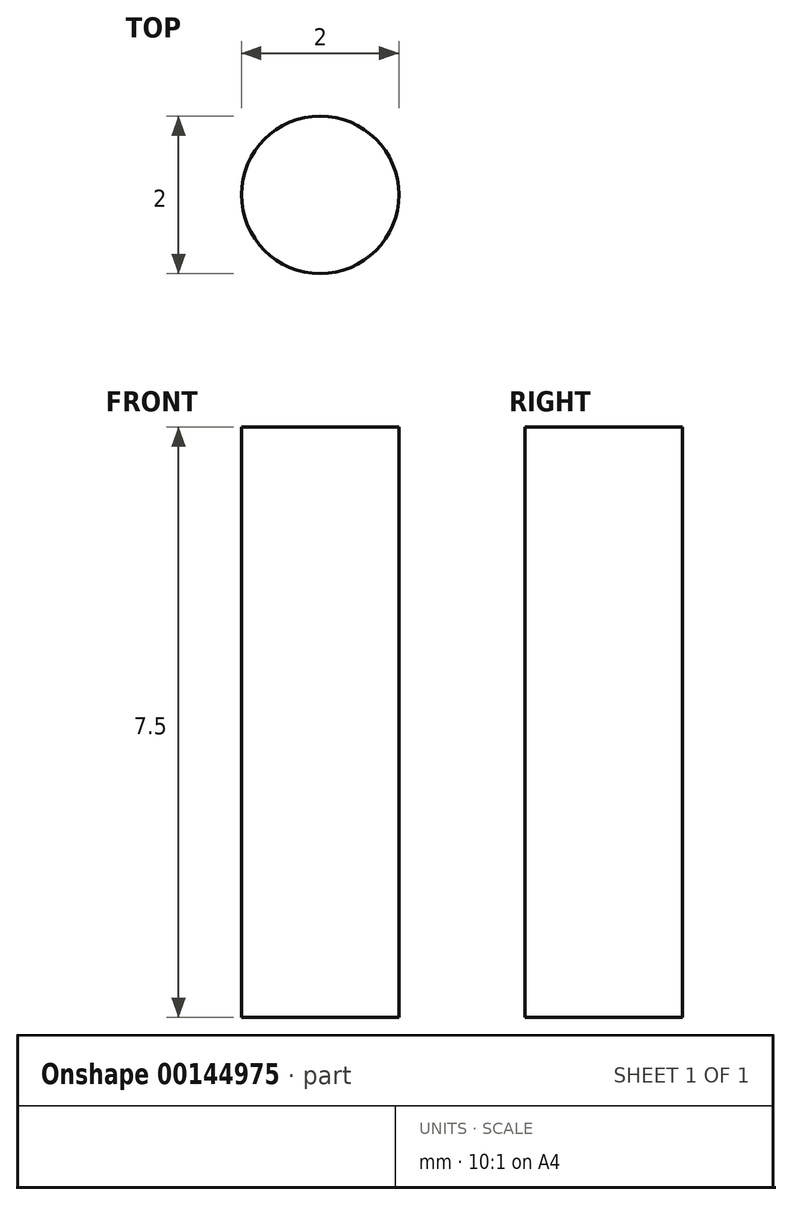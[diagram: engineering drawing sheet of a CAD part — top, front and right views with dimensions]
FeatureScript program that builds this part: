
annotation { "Feature Type Name" : "Feature", "Feature Type Description" : "" }
export const myFeature = defineFeature(function(context is Context, id is Id, definition is map)
    precondition{}
    {
        {
            var Q0;
            Q0=qCreatedBy(makeId("Top.planeOp"),FACE);
            var sketch = newSketch(context, id + "F0", { "sketchPlane" : qUnion([Q0])});
            skCircle(sketch, "E0", {"center": v(0, 0) * mm, "radius": 1 * mm});
            skSolve(sketch);
        }
        {
            var Q0;
            Q0 = qSketchRegion(id + "F0", true);
            extrude(context, id + "F1", {"entities" : qUnion([Q0]), "depth" : 7.5 * mm});
        }
    });
